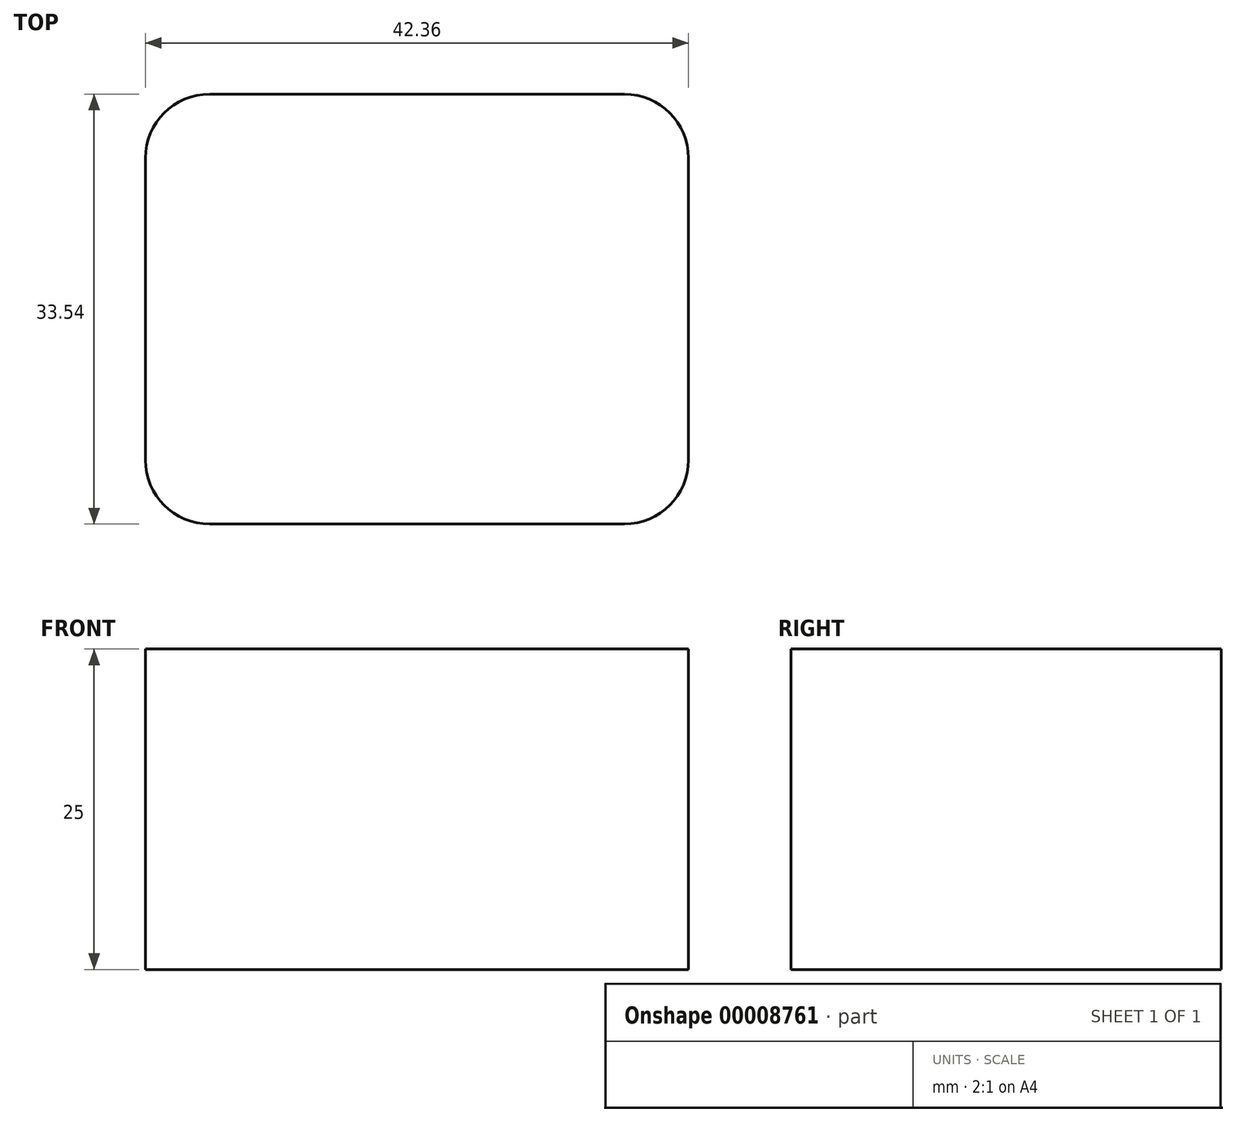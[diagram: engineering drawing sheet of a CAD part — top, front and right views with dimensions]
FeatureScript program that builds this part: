
annotation { "Feature Type Name" : "Feature", "Feature Type Description" : "" }
export const myFeature = defineFeature(function(context is Context, id is Id, definition is map)
    precondition{}
    {
        {
            var Q0;
            Q0=qCreatedBy(makeId("Top.planeOp"),FACE);
            var sketch = newSketch(context, id + "F0", { "sketchPlane" : qUnion([Q0])});
            skLineSegment(sketch, "E0.bottom", {"start": v(-5.53, 0) * mm, "end": v(-47.89, 0) * mm});
            skLineSegment(sketch, "E0.top", {"start": v(-5.53, 33.54) * mm, "end": v(-47.89, 33.54) * mm});
            skLineSegment(sketch, "E0.left", {"start": v(-5.53, 0) * mm, "end": v(-5.53, 33.54) * mm});
            skLineSegment(sketch, "E0.right", {"start": v(-47.89, 0) * mm, "end": v(-47.89, 33.54) * mm});
            skSolve(sketch);
        }
        {
            var Q0;
            Q0 = qSketchRegion(id + "F0", true);
            extrude(context, id + "F1", {"entities" : qUnion([Q0]), "depth" : 25 * mm});
        }
        {
            var Q0;
            Q0=makeQuery(id+"F1.opExtrude","SWEPT_EDGE",EDGE,{"disambiguationData":[OSD([sQuery(id+"F0.wireOp",EDGE,"E0.bottom"),sQuery(id+"F0.wireOp",EDGE,"E0.right")])]});
            var Q1;
            Q1=makeQuery(id+"F1.opExtrude","SWEPT_EDGE",EDGE,{"disambiguationData":[OSD([sQuery(id+"F0.wireOp",EDGE,"E0.bottom"),sQuery(id+"F0.wireOp",EDGE,"E0.left")])]});
            var Q2;
            Q2=makeQuery(id+"F1.opExtrude","SWEPT_EDGE",EDGE,{"disambiguationData":[OSD([sQuery(id+"F0.wireOp",EDGE,"E0.top"),sQuery(id+"F0.wireOp",EDGE,"E0.left")])]});
            var Q3;
            Q3=makeQuery(id+"F1.opExtrude","SWEPT_EDGE",EDGE,{"disambiguationData":[OSD([sQuery(id+"F0.wireOp",EDGE,"E0.top"),sQuery(id+"F0.wireOp",EDGE,"E0.right")])]});
            fillet(context, id + "F2", {"entities" : qUnion([Q0, Q1, Q2, Q3]), "radius" : 5 * mm, "tangentPropagation" : true, "allowEdgeOverflow" : false});
        }
    });
